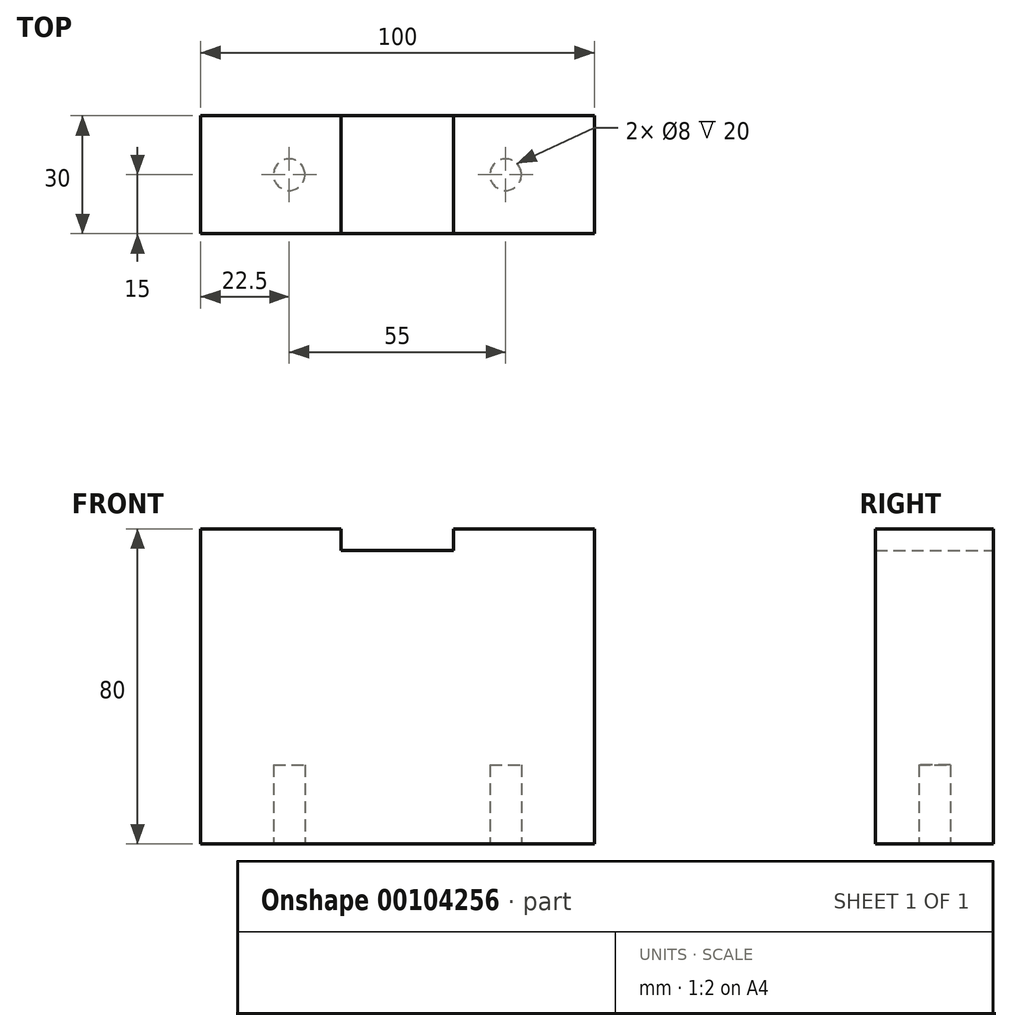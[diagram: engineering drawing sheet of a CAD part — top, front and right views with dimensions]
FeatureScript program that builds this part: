
annotation { "Feature Type Name" : "Feature", "Feature Type Description" : "" }
export const myFeature = defineFeature(function(context is Context, id is Id, definition is map)
    precondition{}
    {
        {
            var Q0;
            Q0=qCreatedBy(makeId("Front.planeOp"),FACE);
            var sketch = newSketch(context, id + "F0", { "sketchPlane" : qUnion([Q0])});
            skLineSegment(sketch, "E0.rect.bottom", {"start": v(50, -51.75) * mm, "end": v(-50, -51.75) * mm, "construction": true});
            skLineSegment(sketch, "E0.rect.top", {"start": v(50, 51.75) * mm, "end": v(-50, 51.75) * mm, "construction": true});
            skLineSegment(sketch, "E0.rect.left", {"start": v(50, -51.75) * mm, "end": v(50, 51.75) * mm, "construction": true});
            skLineSegment(sketch, "E0.rect.right", {"start": v(-50, -51.75) * mm, "end": v(-50, 51.75) * mm, "construction": true});
            skPoint(sketch, "E0.rect.middle", {"position": v(0, 0) * mm});
            skCircle(sketch, "E1", {"center": v(0, 51.75) * mm, "radius": 27.5 * mm, "construction": true});
            skLineSegment(sketch, "E2.bottom", {"start": v(-50, -51.75) * mm, "end": v(50, -51.75) * mm});
            skLineSegment(sketch, "E2.top", {"start": v(-50, 28.25) * mm, "end": v(-14.28, 28.25) * mm});
            skLineSegment(sketch, "E2.left", {"start": v(-50, -51.75) * mm, "end": v(-50, 28.25) * mm});
            skLineSegment(sketch, "E2.right", {"start": v(50, -51.75) * mm, "end": v(50, 28.25) * mm});
            skPoint(sketch, "E3", {"position": v(14.28, 28.25) * mm});
            skPoint(sketch, "E4", {"position": v(-14.28, 28.25) * mm});
            skLineSegment(sketch, "E5.top", {"start": v(14.28, 22.75) * mm, "end": v(-14.28, 22.75) * mm});
            skLineSegment(sketch, "E5.left", {"start": v(14.28, 28.25) * mm, "end": v(14.28, 22.75) * mm});
            skLineSegment(sketch, "E5.right", {"start": v(-14.28, 28.25) * mm, "end": v(-14.28, 22.75) * mm});
            skLineSegment(sketch, "E6.trimOffspring", {"start": v(14.28, 28.25) * mm, "end": v(50, 28.25) * mm});
            skSolve(sketch);
        }
        {
            var Q0;
            Q0=qSketchRegion(id+"F0",true);
            extrude(context, id + "F1", {"entities" : qUnion([Q0]), "depth" : 30 * mm});
        }
        {
            var Q0;
            Q0=makeQuery(id+"F1.opExtrude","SWEPT_FACE",FACE,{"disambiguationData":[OSD([sQuery(id+"F0.wireOp",EDGE,"E2.bottom")])]});
            var sketch = newSketch(context, id + "F2", { "sketchPlane" : qUnion([Q0])});
            skCircle(sketch, "E7", {"center": v(-27.5, 15) * mm, "radius": 4 * mm});
            skCircle(sketch, "E8", {"center": v(27.5, 15) * mm, "radius": 4 * mm});
            skSolve(sketch);
        }
        {
            var Q0;
            Q0 = qSketchRegion(id + "F2", true);
            extrude(context, id + "F3", {"entities" : qUnion([Q0]), "operationType" : NewBodyOperationType.REMOVE, "oppositeDirection" : true, "depth" : 20 * mm});
        }
    });
